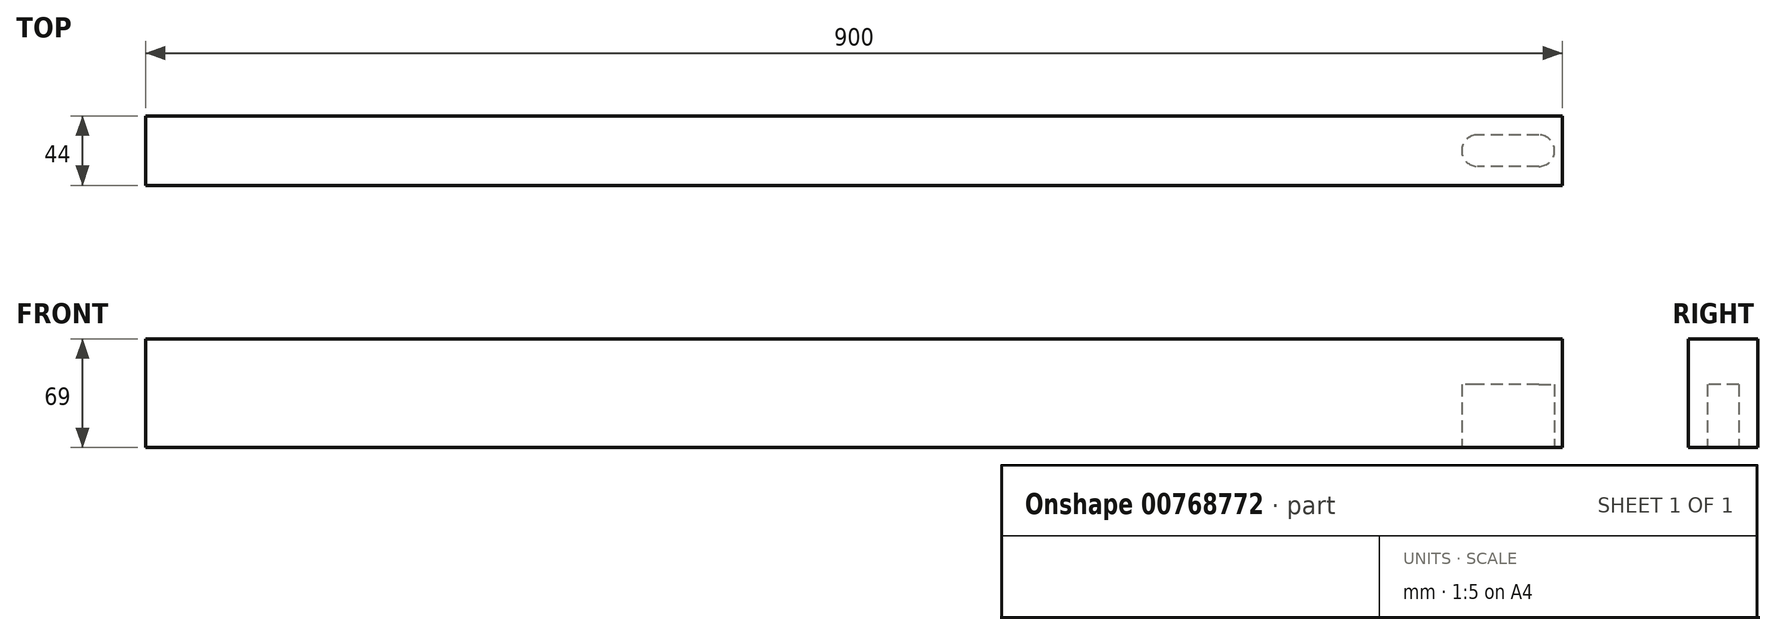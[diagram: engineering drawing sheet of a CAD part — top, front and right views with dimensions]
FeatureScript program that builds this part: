
annotation { "Feature Type Name" : "Feature", "Feature Type Description" : "" }
export const myFeature = defineFeature(function(context is Context, id is Id, definition is map)
    precondition{}
    {
        {
            var Q0;
            Q0=qCreatedBy(makeId("Right.planeOp"),FACE);
            var sketch = newSketch(context, id + "F0", { "sketchPlane" : qUnion([Q0])});
            skLineSegment(sketch, "E0.bottom", {"start": v(-20.48, 69) * mm, "end": v(23.52, 69) * mm});
            skLineSegment(sketch, "E0.top", {"start": v(-20.48, 0) * mm, "end": v(23.52, 0) * mm});
            skLineSegment(sketch, "E0.left", {"start": v(-20.48, 69) * mm, "end": v(-20.48, 0) * mm});
            skLineSegment(sketch, "E0.right", {"start": v(23.52, 69) * mm, "end": v(23.52, 0) * mm});
            skSolve(sketch);
        }
        {
            var Q0;
            Q0=makeQuery(id+"F0.imprint","IMPRINT",FACE,{"disambiguationData":[TD([[makeQuery(id+"F0.imprint","IMPRINT",EDGE,{"derivedFrom":sQuery(id+"F0.wireOp",EDGE,"E0.bottom")}),-1.0]])]});
            extrude(context, id + "F1", {"entities" : qUnion([Q0]), "depth" : 900 * mm, "offsetDistance" : 25 * mm});
        }
        {
            var Q0;
            Q0=makeQuery(id+"F1.opExtrude","SWEPT_FACE",FACE,{"disambiguationData":[OSD([sQuery(id+"F0.wireOp",EDGE,"E0.top")])]});
            var sketch = newSketch(context, id + "F2", { "sketchPlane" : qUnion([Q0])});
            skLineSegment(sketch, "E1.bottom", {"start": v(885, 8.48) * mm, "end": v(846, 8.48) * mm});
            skLineSegment(sketch, "E1.top", {"start": v(885, -11.52) * mm, "end": v(846, -11.52) * mm});
            skArc(sketch, "E2", {"start": v(885, -11.52) * mm, "mid": v(895, -1.52) * mm, "end": v(885, 8.48) * mm});
            skArc(sketch, "E3", {"start": v(846, 8.48) * mm, "mid": v(836, -1.52) * mm, "end": v(846, -11.52) * mm});
            skSolve(sketch);
        }
        {
            var Q0;
            Q0=makeQuery(id+"F2.imprint","IMPRINT",FACE,{"disambiguationData":[TD([[makeQuery(id+"F2.imprint","IMPRINT",EDGE,{"derivedFrom":sQuery(id+"F2.wireOp",EDGE,"E1.bottom")}),1.0]])]});
            extrude(context, id + "F3", {"entities" : qUnion([Q0]), "operationType" : NewBodyOperationType.REMOVE, "oppositeDirection" : true, "depth" : 40 * mm, "offsetDistance" : 25 * mm});
        }
    });
